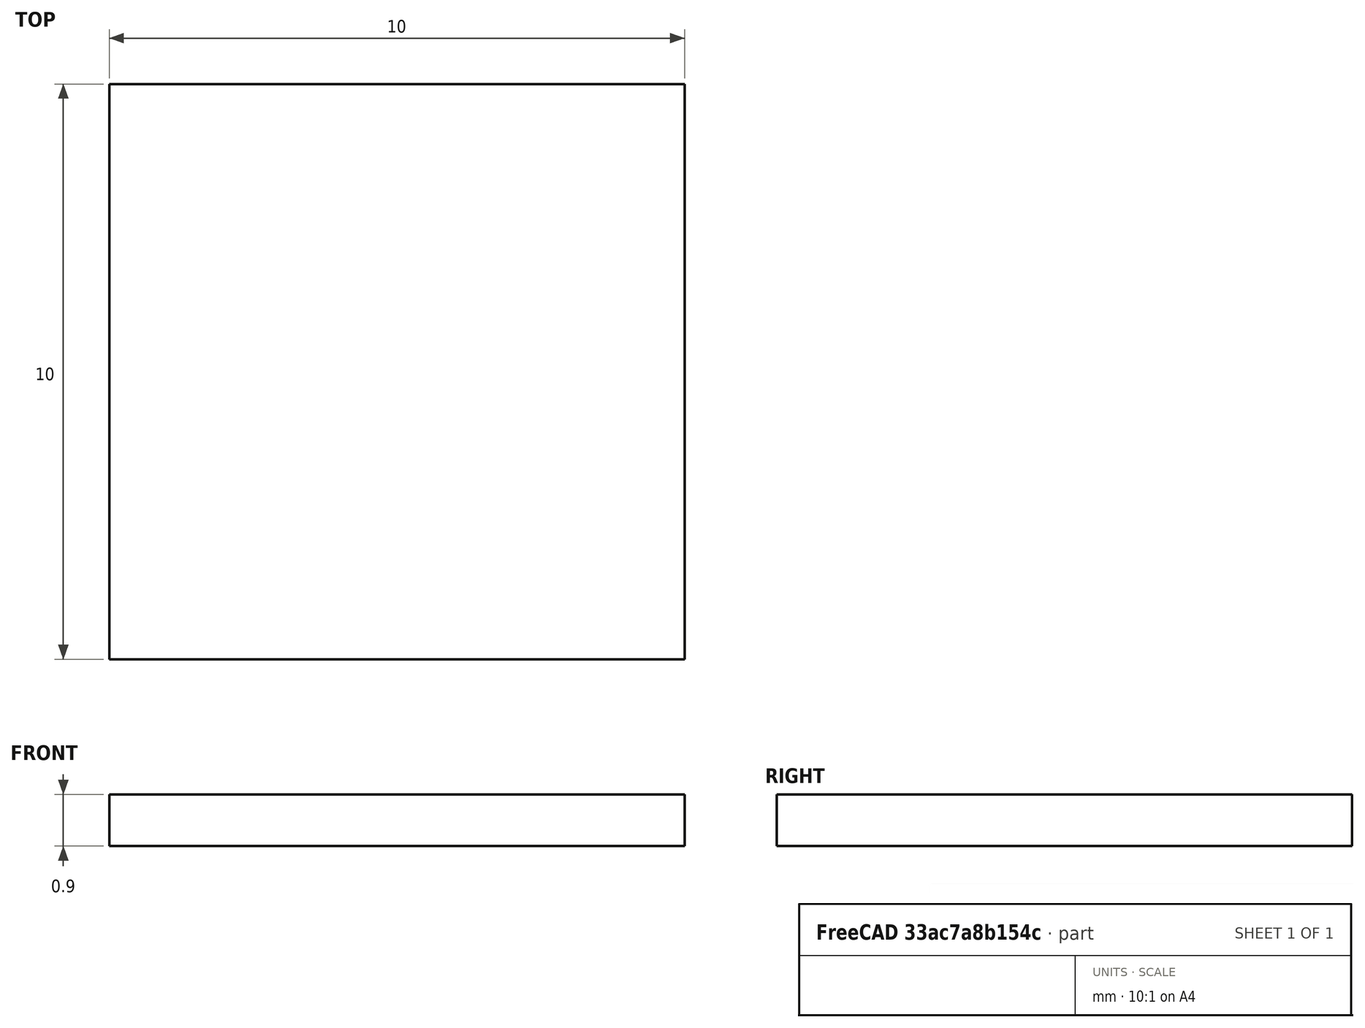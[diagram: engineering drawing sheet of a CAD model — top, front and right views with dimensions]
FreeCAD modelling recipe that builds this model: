
FCSTD DOCUMENT  (FreeCAD 0.18R16146 (Git))
Label: gowin
License: All rights reserved
LicenseURL: http://en.wikipedia.org/wiki/All_rights_reserved
objects: Sketcher::SketchObject×1, PartDesign::Body×1, Part::Extrusion×1
note: 3 computed .brp shape members not serialized (recipe doc carries the construction recipe); baked Part::Feature solids carry a one-line shape summary decoded from their .brp

FEATURE [Sketcher::SketchObject] Sketch
  MapMode = 5
  Support = -> [XY_Plane]
  sketch-geometry (6):
    g0: LineSegment StartX=0 StartY=10 StartZ=0 EndX=10 EndY=10 EndZ=0
    g1: LineSegment StartX=10 StartY=10 StartZ=0 EndX=10 EndY=0 EndZ=0
    g2: LineSegment StartX=10 StartY=0 StartZ=0 EndX=0 EndY=0 EndZ=0
    g3: LineSegment StartX=0 StartY=0 StartZ=0 EndX=0 EndY=10 EndZ=0
    g4: GeomPoint X=0 Y=0 Z=0
    g5: GeomPoint X=0 Y=0 Z=0
  constraints (13):
    c: Coincident(g0,g1)
    c: Coincident(g1,g2)
    c: Coincident(g2,g3)
    c: Coincident(g3,g0)
    c: Horizontal(g0)
    c: Horizontal(g2)
    c: Vertical(g1)
    c: Vertical(g3)
    c: DistanceY(g1,g1) = 10
    c: DistanceX(g0,g0) = 10
    c: Coincident(g4,g2)
    c: Coincident(g5,g-1)
    c: Coincident(g5,g2)
FEATURE [PartDesign::Body] Body
  Group = -> [Sketch]
  Origin = -> Origin
FEATURE [Part::Extrusion] Extrude
  Base = -> Sketch
  Dir = (0,0,1)
  DirMode = 2
  FaceMakerClass = Part::FaceMakerBullseye
  LengthFwd = 0.9
  LengthRev = 0
  Solid = true
  Symmetric = false
